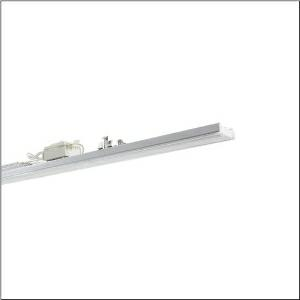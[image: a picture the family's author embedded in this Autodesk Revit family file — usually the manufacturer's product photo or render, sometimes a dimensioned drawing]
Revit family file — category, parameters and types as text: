
# Revit family: licross_11_recessed_mo_51tl1edn495g
name_source: partatom
category: Lighting Fixtures
units: mm (PartAtom-declared; Revit-internal decimal feet)

## family parameters
Cut with Voids When Loaded = No
Host = Face
Light Source = No
Part Type = Normal
Room Calculation Point = No
Round Connector Dimension = Use Diameter
Shared = No

## types (1)
- --- (1 x LED, 9900 lm, 56.7 W, 4000K)
    Apparent Load = 57 VA
    CIE Flux Codes = 85 95 99 100 100
    Color Rendering = 80
    Color Temperature = 4000K
    Default Elevation = 1800 mm
    Description = Licross 11 Recessed MO, luminaire insert, of sheet steel, coil coated, white, length: 1.500mm, width: 66mm, height: 67mm, LED rated luminous flux: 9.900lm, light colour: 840, SDCM (Standard Deviation of Colour Matching)MacAdam ≤ 2 SDCM (initial), control gear: DALI 2, with plug, 5-pole, with phase selection, mains connection: 220..240V, AC, 50/60Hz, rated input power: 57W, internal wiring halogen-free, primary light control with lens, of plastic, primary optical cover: cover, of PMMA, light emission: direct distribution, primary light characteristic: symmetric, protection rating (complete): IP40, insulation class (complete): insulation class I (protective earthing), certification: CE, ENEC, VDE, UKCA, protection symbol: D if used in an environment without relevant dust loads with corresponding accessories, impact resistance: IK06, permissible ambient temperature for indoor applications: -25..+35°C, corresponds to IFS (International Featured Standards) requirements for safety and quality in the food industry, reducing of maximum allowable ambient temperature of 5°C with ceiling mounting, LABS conformity tested according to VDMA 24364:2018-05, The light source and the operating device comply with the requirements of the Ecodesign Regulation (EU) 2019/2020 and are replaceable in accordance with this regulation, packaging unit: 1 piece
    Height = 58 mm
    Lamp = 1 x LED
    Lamp Light Flux = 9900 lm
    Lamp Power = 56.7 W
    Lamp count = 1
    Length = 1500 mm
    Luminous efficacy = 175 lm/W
    Manufacturer = Siteco
    ModVariant = No
    Model = 51TL1EDN495G
    Mounting Place = Ceiling
    Mounting Type = Pendant
    Number of Poles = 1
    OnlyDefault = Yes
    Power Factor = 1
    Product Name = Licross 11 Recessed MO
    Product group = luminaire insert | ceiling pendant
    ProductGroupID = 901
    Protection Class = Protection class I
    Protection Degree = IP 40
    RLX_Detail_Level = 1
    RLX_Emergency_Light_Flux = 0 lm
    RLX_Emergency_Type = 0
    RLX_Emergency_Type_DB = No
    RlxData = <blob elided: 24837 chars, md5=8d8938b0>
    Socket = socket
    Standby Power = 0 W
    System Light Flux = 9900 lm
    System Power = 57 W
    Type Comments = factory setting: luminous flux: 100 % | dim-lin: 254 | 378 mA
    Type Image = l_1296930.jpg
    URL = http://relux.com
    VarID = @adj_099897
    Voltage = 0 V
    Weight = 0.00 kg
    Width = 66 mm

## geometry (parser evidence)
native form markers: Blend x4, Sweep x12
no freeform markers — native parametric forms only
